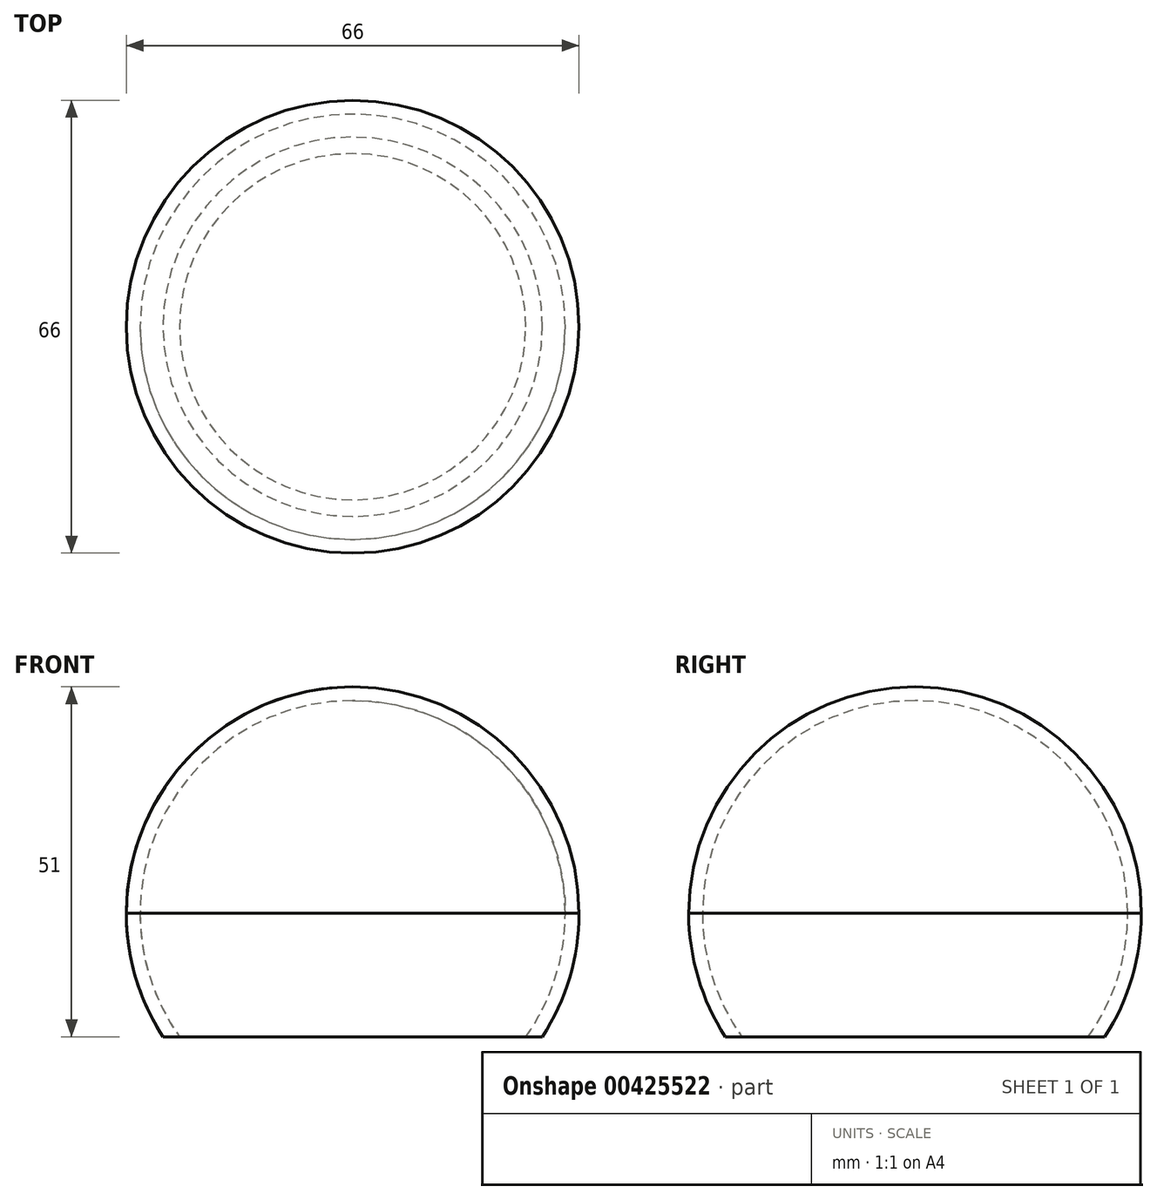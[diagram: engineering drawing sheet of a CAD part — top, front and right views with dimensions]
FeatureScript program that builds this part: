
annotation { "Feature Type Name" : "Feature", "Feature Type Description" : "" }
export const myFeature = defineFeature(function(context is Context, id is Id, definition is map)
    precondition{}
    {
        {
            var Q0;
            Q0=qCreatedBy(makeId("Front.planeOp"),FACE);
            var sketch = newSketch(context, id + "F0", { "sketchPlane" : qUnion([Q0])});
            skArc(sketch, "E0", {"start": v(0, 33) * mm, "mid": v(-23.33, 23.33) * mm, "end": v(-33, 0) * mm});
            skLineSegment(sketch, "E1", {"start": v(-28.47, 0) * mm, "end": v(32.47, 0) * mm, "construction": true});
            skLineSegment(sketch, "E2", {"start": v(0, 0) * mm, "end": v(0, 50.31) * mm, "construction": true});
            skArc(sketch, "E3.0", {"start": v(0, 31) * mm, "mid": v(-21.92, 21.92) * mm, "end": v(-31, 0) * mm});
            skLineSegment(sketch, "E4", {"start": v(0, 33) * mm, "end": v(0, 31) * mm});
            skLineSegment(sketch, "E5", {"start": v(-31, 0) * mm, "end": v(-33, 0) * mm});
            skSolve(sketch);
        }
        {
            var Q0;
            Q0 = qSketchRegion(id + "F0", true);
            var Q1;
            Q1=sQuery(id+"F0.wireOp",EDGE,"E2");
            revolve(context, id + "F1", {"entities" : qUnion([Q0]), "axis" : qUnion([Q1]), "revolveType" : RevolveType.FULL});
        }
        {
            var Q0;
            Q0=qCreatedBy(makeId("Front.planeOp"),FACE);
            var sketch = newSketch(context, id + "F2", { "sketchPlane" : qUnion([Q0])});
            skArc(sketch, "E6.0", {"start": v(-33, 0) * mm, "mid": v(-23.33, -23.33) * mm, "end": v(0, -33) * mm});
            skLineSegment(sketch, "E7", {"start": v(0, 0) * mm, "end": v(0, -49.99) * mm, "construction": true});
            skPoint(sketch, "E8.orphan", {"position": v(-33, 0) * mm});
            skLineSegment(sketch, "E9", {"start": v(0, 0) * mm, "end": v(-52.44, 0) * mm});
            skPoint(sketch, "E10.orphan", {"position": v(0, 33) * mm});
            skArc(sketch, "E11.0", {"start": v(-31, 0) * mm, "mid": v(-21.92, -21.92) * mm, "end": v(0, -31) * mm});
            skLineSegment(sketch, "E12", {"start": v(33.02, -18) * mm, "end": v(-59.39, -18) * mm});
            skSolve(sketch);
        }
        {
            var Q0;
            Q0 = qSketchRegion(id + "F2", true);
            var Q1;
            Q1=sQuery(id+"F0.wireOp",EDGE,"E2");
            revolve(context, id + "F3", {"entities" : qUnion([Q0]), "axis" : qUnion([Q1]), "revolveType" : RevolveType.FULL});
        }
    });
